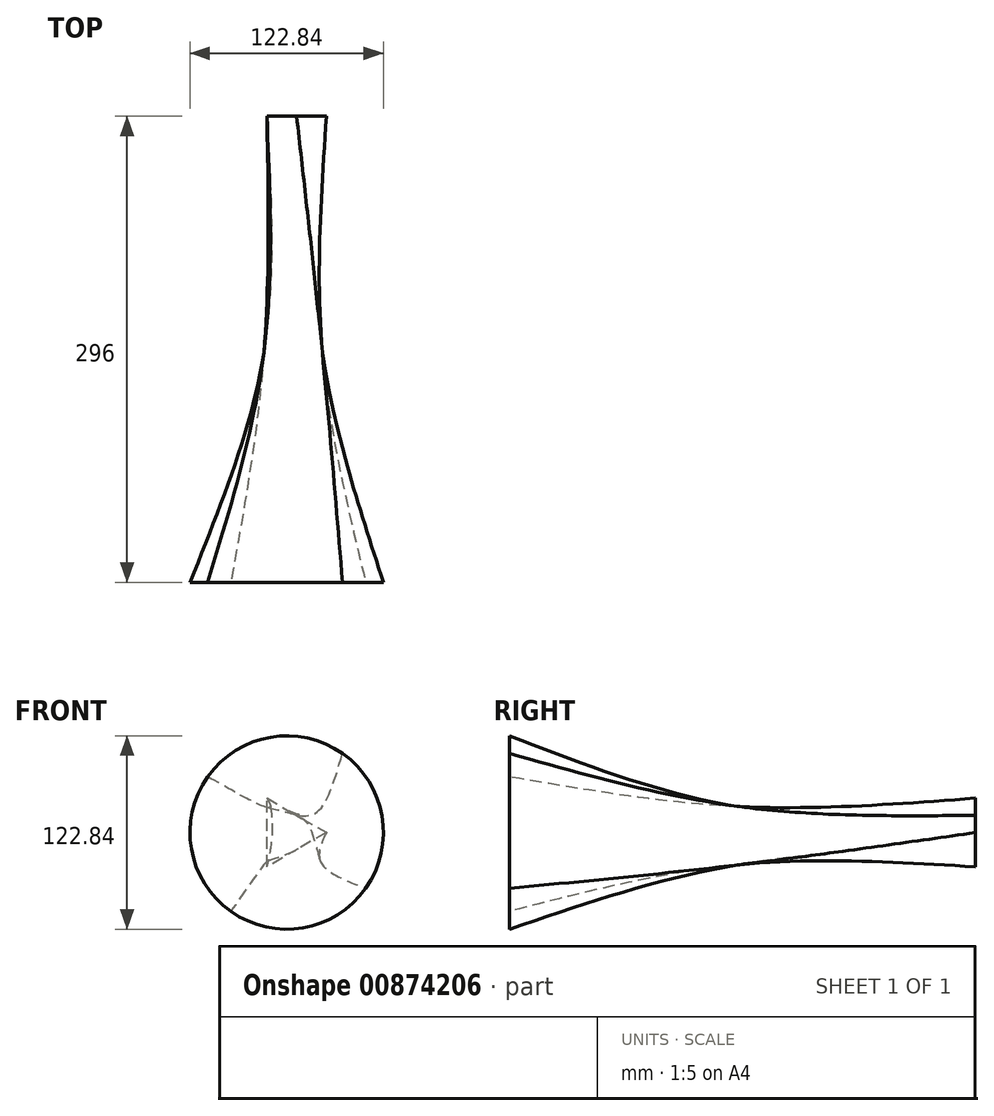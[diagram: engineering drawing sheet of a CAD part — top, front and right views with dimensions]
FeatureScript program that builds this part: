
annotation { "Feature Type Name" : "Feature", "Feature Type Description" : "" }
export const myFeature = defineFeature(function(context is Context, id is Id, definition is map)
    precondition{}
    {
        {
            var Q0;
            Q0=qCreatedBy(makeId("Front.planeOp"),FACE);
            cPlane(context, id + "F0", {"entities" : qUnion([Q0]), "cplaneType" : CPlaneType.OFFSET, "offset" : 146 * mm, "width" : 150 * mm, "height" : 150 * mm});
        }
        {
            var Q0;
            Q0=qCreatedBy(id+"F0.planeOp",FACE);
            var sketch = newSketch(context, id + "F1", { "sketchPlane" : qUnion([Q0])});
            skCircle(sketch, "E0", {"center": v(0, 0) * mm, "radius": 61.42 * mm});
            skSolve(sketch);
        }
        {
            var Q0;
            Q0=qCreatedBy(makeId("Front.planeOp"),FACE);
            var sketch = newSketch(context, id + "F2", { "sketchPlane" : qUnion([Q0])});
            skLineSegment(sketch, "E1.bottom", {"start": v(-14.43, 16.42) * mm, "end": v(22.6, 16.42) * mm});
            skLineSegment(sketch, "E1.top", {"start": v(-14.43, -20.41) * mm, "end": v(22.6, -20.41) * mm});
            skLineSegment(sketch, "E1.left", {"start": v(-14.43, 16.42) * mm, "end": v(-14.43, -20.41) * mm});
            skLineSegment(sketch, "E1.right", {"start": v(22.6, 16.42) * mm, "end": v(22.6, -20.41) * mm});
            skSolve(sketch);
        }
        {
            var Q0;
            Q0=qCreatedBy(makeId("Front.planeOp"),FACE);
            cPlane(context, id + "F3", {"entities" : qUnion([Q0]), "cplaneType" : CPlaneType.OFFSET, "offset" : 150 * mm, "oppositeDirection" : true, "width" : 150 * mm, "height" : 150 * mm});
        }
        {
            var Q0;
            Q0=qCreatedBy(id+"F3.planeOp",FACE);
            var sketch = newSketch(context, id + "F4", { "sketchPlane" : qUnion([Q0])});
            skCircle(sketch, "E2.cCircle", {"center": v(0, 0) * mm, "radius": 12.6 * mm, "construction": true});
            skLineSegment(sketch, "E2.0", {"start": v(-12.6, -21.83) * mm, "end": v(-12.6, 21.83) * mm});
            skLineSegment(sketch, "E2.1", {"start": v(-12.6, 21.83) * mm, "end": v(25.2, 0) * mm});
            skLineSegment(sketch, "E2.2", {"start": v(25.2, 0) * mm, "end": v(-12.6, -21.83) * mm});
            skPoint(sketch, "E2.0.midPoint", {"position": v(-12.6, 0) * mm});
            skSolve(sketch);
        }
        {
            var Q0;
            Q0=makeQuery(id+"F4.imprint","IMPRINT",FACE,{"disambiguationData":[TD([[makeQuery(id+"F4.imprint","IMPRINT",EDGE,{"derivedFrom":sQuery(id+"F4.wireOp",EDGE,"E2.0")}),-1.0]])]});
            var Q1;
            Q1=makeQuery(id+"F2.imprint","IMPRINT",FACE,{"disambiguationData":[TD([[makeQuery(id+"F2.imprint","IMPRINT",EDGE,{"derivedFrom":sQuery(id+"F2.wireOp",EDGE,"E1.bottom")}),-1.0]])]});
            var Q2;
            Q2=makeQuery(id+"F1.imprint","IMPRINT",FACE,{"disambiguationData":[TD([[makeQuery(id+"F1.imprint","IMPRINT",EDGE,{"derivedFrom":sQuery(id+"F1.wireOp",EDGE,"E0")}),1.0]])]});
            loft(context, id + "F5", {"sheetProfilesArray" : [{ "sheetProfileEntities" : qUnion([Q0]) }, { "sheetProfileEntities" : qUnion([Q1]) }, { "sheetProfileEntities" : qUnion([Q2]) }]});
        }
    });
